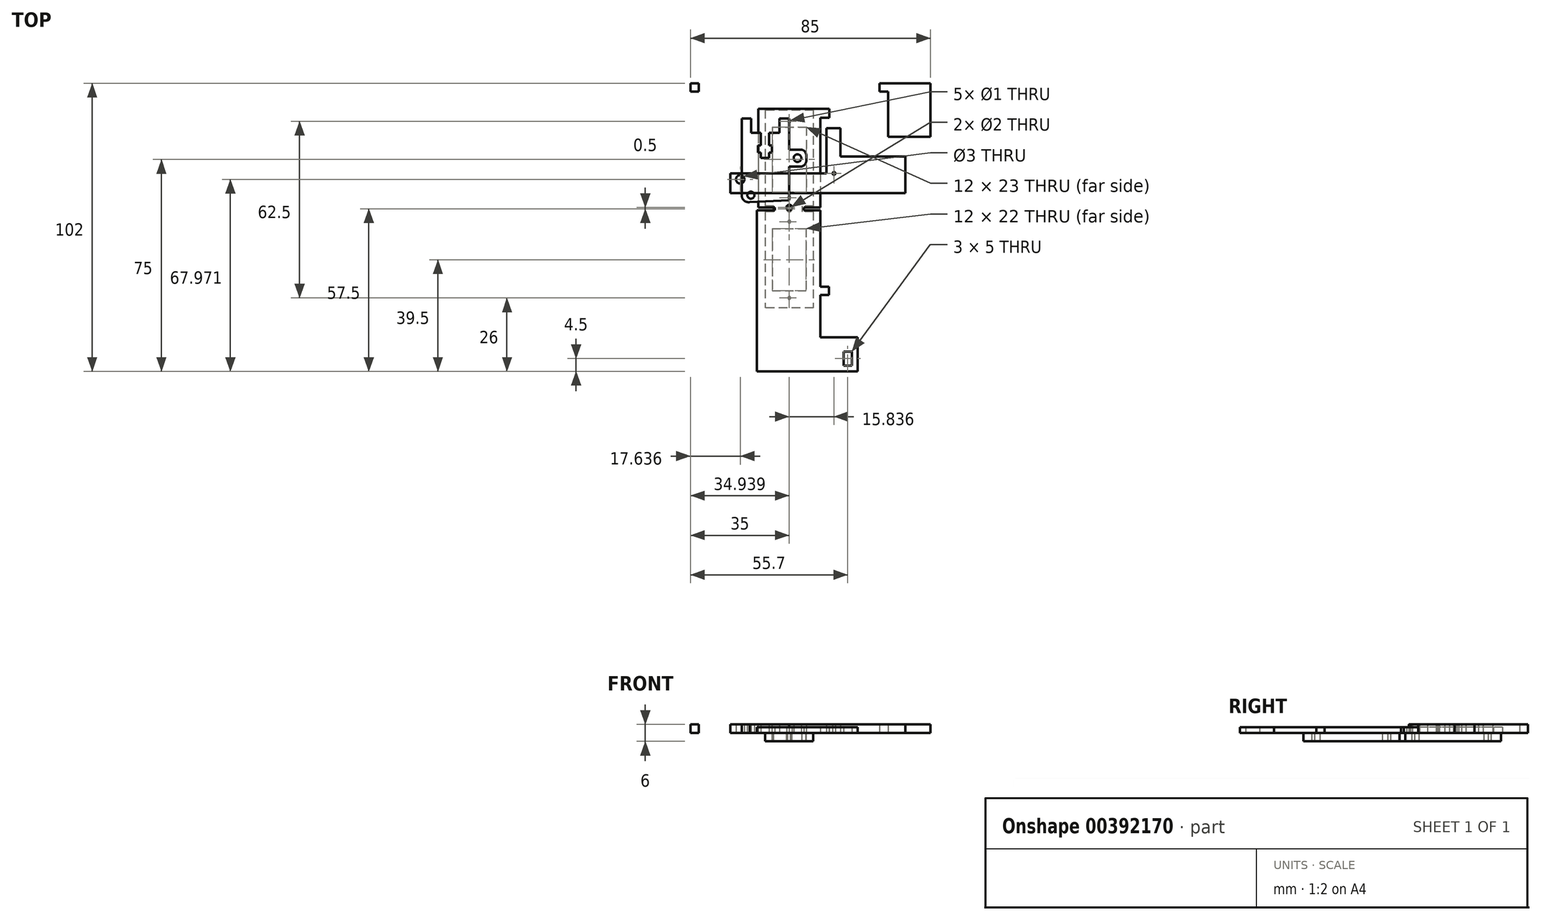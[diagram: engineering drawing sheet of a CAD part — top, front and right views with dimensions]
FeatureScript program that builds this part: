
annotation { "Feature Type Name" : "Feature", "Feature Type Description" : "" }
export const myFeature = defineFeature(function(context is Context, id is Id, definition is map)
    precondition{}
    {
        {
            var Q0;
            Q0=qCreatedBy(makeId("Top.planeOp"),FACE);
            var sketch = newSketch(context, id + "F0", { "sketchPlane" : qUnion([Q0])});
            skLineSegment(sketch, "E0.bottom", {"start": v(11, 17.5) * mm, "end": v(-11, 17.5) * mm});
            skLineSegment(sketch, "E0.top", {"start": v(11, -17.5) * mm, "end": v(-11, -17.5) * mm});
            skLineSegment(sketch, "E0.left", {"start": v(11, 17.5) * mm, "end": v(11, -17.5) * mm});
            skLineSegment(sketch, "E0.right", {"start": v(-11, 17.5) * mm, "end": v(-11, -17.5) * mm});
            skPoint(sketch, "E0.middle", {"position": v(0, 0) * mm});
            skLineSegment(sketch, "E1.bottom", {"start": v(11, 17.5) * mm, "end": v(14.2, 17.5) * mm});
            skLineSegment(sketch, "E1.top", {"start": v(11, 14.3) * mm, "end": v(14.2, 14.3) * mm});
            skLineSegment(sketch, "E1.left", {"start": v(11, 17.5) * mm, "end": v(11, 14.3) * mm});
            skLineSegment(sketch, "E1.right", {"start": v(14.2, 17.5) * mm, "end": v(14.2, 14.3) * mm});
            skLineSegment(sketch, "E2.bottom", {"start": v(5.1, -18.5) * mm, "end": v(-5.1, -18.5) * mm});
            skLineSegment(sketch, "E2.top", {"start": v(5.1, -16.5) * mm, "end": v(-5.1, -16.5) * mm});
            skLineSegment(sketch, "E2.left", {"start": v(5.1, -18.5) * mm, "end": v(5.1, -16.5) * mm});
            skLineSegment(sketch, "E2.right", {"start": v(-5.1, -18.5) * mm, "end": v(-5.1, -16.5) * mm});
            skPoint(sketch, "E2.middle", {"position": v(0, -17.5) * mm});
            skLineSegment(sketch, "E3.bottom", {"start": v(11, -18.5) * mm, "end": v(-11.53, -18.5) * mm});
            skLineSegment(sketch, "E3.top", {"start": v(11, -75.5) * mm, "end": v(-11.53, -75.5) * mm});
            skLineSegment(sketch, "E3.left", {"start": v(11, -18.5) * mm, "end": v(11, -75.5) * mm});
            skLineSegment(sketch, "E3.right", {"start": v(-11.53, -18.5) * mm, "end": v(-11.53, -75.5) * mm});
            skLineSegment(sketch, "E4.bottom", {"start": v(11, -75.5) * mm, "end": v(24.2, -75.5) * mm});
            skLineSegment(sketch, "E4.top", {"start": v(11, -63.5) * mm, "end": v(24.2, -63.5) * mm});
            skLineSegment(sketch, "E4.left", {"start": v(11, -75.5) * mm, "end": v(11, -63.5) * mm});
            skLineSegment(sketch, "E4.right", {"start": v(24.2, -75.5) * mm, "end": v(24.2, -63.5) * mm});
            skLineSegment(sketch, "E5.bottom", {"start": v(11, -45.5) * mm, "end": v(14, -45.5) * mm});
            skLineSegment(sketch, "E5.top", {"start": v(11, -48.5) * mm, "end": v(14, -48.5) * mm});
            skLineSegment(sketch, "E5.left", {"start": v(11, -45.5) * mm, "end": v(11, -48.5) * mm});
            skLineSegment(sketch, "E5.right", {"start": v(14, -45.5) * mm, "end": v(14, -48.5) * mm});
            skLineSegment(sketch, "E6.bottom", {"start": v(22.2, -73.5) * mm, "end": v(19.2, -73.5) * mm});
            skLineSegment(sketch, "E6.top", {"start": v(22.2, -68.5) * mm, "end": v(19.2, -68.5) * mm});
            skLineSegment(sketch, "E6.left", {"start": v(22.2, -73.5) * mm, "end": v(22.2, -68.5) * mm});
            skLineSegment(sketch, "E6.right", {"start": v(19.2, -73.5) * mm, "end": v(19.2, -68.5) * mm});
            skPoint(sketch, "E6.middle", {"position": v(20.7, -71) * mm});
            skCircle(sketch, "E7", {"center": v(0, -17.5) * mm, "radius": 1 * mm});
            skSolve(sketch);
        }
        {
            var Q0;
            Q0=makeQuery(id+"F0.imprint","IMPRINT",FACE,{"disambiguationData":[TD([[makeQuery(id+"F0.imprint","IMPRINT",EDGE,{"derivedFrom":sQuery(id+"F0.wireOp",EDGE,"E3.top")}),-1.0]])]});
            var Q1;
            Q1=makeQuery(id+"F0.imprint","IMPRINT",FACE,{"disambiguationData":[TD([[makeQuery(id+"F0.imprint","IMPRINT",EDGE,{"derivedFrom":sQuery(id+"F0.wireOp",EDGE,"E4.bottom")}),1.0]])]});
            var Q2;
            Q2=makeQuery(id+"F0.imprint","IMPRINT",FACE,{"disambiguationData":[TD([[makeQuery(id+"F0.imprint","IMPRINT",EDGE,{"derivedFrom":sQuery(id+"F0.wireOp",EDGE,"E5.bottom")}),-1.0]])]});
            var Q3;
            Q3=makeQuery(id+"F0.imprint","IMPRINT",FACE,{"disambiguationData":[TD([[makeQuery(id+"F0.imprint","IMPRINT",EDGE,{"derivedFrom":sQuery(id+"F0.wireOp",EDGE,"E0.bottom")}),1.0]])]});
            var Q4;
            Q4=makeQuery(id+"F0.imprint","IMPRINT",FACE,{"disambiguationData":[TD([[makeQuery(id+"F0.imprint","IMPRINT",EDGE,{"derivedFrom":sQuery(id+"F0.wireOp",EDGE,"E1.bottom")}),-1.0]])]});
            var Q5;
            {var subQ0=sQuery(id+"F0.wireOp",EDGE,"E2.left");var subQ1=sQuery(id+"F0.wireOp",EDGE,"E0.top");var subQ2=makeQuery(id+"F0.imprint","INTERSECT",VERTEX,{"derivedFrom":[subQ1,subQ0]});Q5=makeQuery(id+"F0.imprint","IMPRINT",FACE,{"disambiguationData":[TD([[makeQuery(id+"F0.imprint","IMPRINT",EDGE,{"disambiguationData":[TD([[subQ2,-1.0]])],"derivedFrom":subQ1}),1.0]])]});}
            var Q6;
            {var subQ0=sQuery(id+"F0.wireOp",EDGE,"E2.left");var subQ1=sQuery(id+"F0.wireOp",EDGE,"E0.top");var subQ2=makeQuery(id+"F0.imprint","INTERSECT",VERTEX,{"derivedFrom":[subQ1,subQ0]});Q6=makeQuery(id+"F0.imprint","IMPRINT",FACE,{"disambiguationData":[TD([[makeQuery(id+"F0.imprint","IMPRINT",EDGE,{"disambiguationData":[TD([[subQ2,-1.0]])],"derivedFrom":subQ1}),-1.0]])]});}
            var Q7;
            {var subQ0=sQuery(id+"F0.wireOp",EDGE,"E2.right");var subQ1=sQuery(id+"F0.wireOp",EDGE,"E0.top");var subQ2=makeQuery(id+"F0.imprint","INTERSECT",VERTEX,{"derivedFrom":[subQ1,subQ0]});Q7=makeQuery(id+"F0.imprint","IMPRINT",FACE,{"disambiguationData":[TD([[makeQuery(id+"F0.imprint","IMPRINT",EDGE,{"disambiguationData":[TD([[subQ2,1.0]])],"derivedFrom":subQ1}),1.0]])]});}
            var Q8;
            {var subQ0=sQuery(id+"F0.wireOp",EDGE,"E2.right");var subQ1=sQuery(id+"F0.wireOp",EDGE,"E0.top");var subQ2=makeQuery(id+"F0.imprint","INTERSECT",VERTEX,{"derivedFrom":[subQ1,subQ0]});Q8=makeQuery(id+"F0.imprint","IMPRINT",FACE,{"disambiguationData":[TD([[makeQuery(id+"F0.imprint","IMPRINT",EDGE,{"disambiguationData":[TD([[subQ2,1.0]])],"derivedFrom":subQ1}),-1.0]])]});}
            extrude(context, id + "F1", {"entities" : qUnion([Q0, Q1, Q2, Q3, Q4, Q5, Q6, Q7, Q8]), "depth" : 2 * mm});
        }
        {
            var Q0;
            Q0=qCreatedBy(makeId("Top.planeOp"),FACE);
            var sketch = newSketch(context, id + "F2", { "sketchPlane" : qUnion([Q0])});
            skLineSegment(sketch, "E8.top", {"start": v(35, 26.5) * mm, "end": v(-35, 26.5) * mm});
            skLineSegment(sketch, "E8.left", {"start": v(35, -26.5) * mm, "end": v(35, 26.5) * mm});
            skLineSegment(sketch, "E8.right", {"start": v(-35, -26.5) * mm, "end": v(-35, 26.5) * mm});
            skPoint(sketch, "E8.middle", {"position": v(0, 0) * mm});
            skLineSegment(sketch, "E9.bottom", {"start": v(35, 26.5) * mm, "end": v(50, 26.5) * mm});
            skLineSegment(sketch, "E9.top", {"start": v(35, 7.5) * mm, "end": v(50, 7.5) * mm});
            skLineSegment(sketch, "E9.left", {"start": v(35, 26.5) * mm, "end": v(35, 7.5) * mm});
            skLineSegment(sketch, "E9.right", {"start": v(50, 26.5) * mm, "end": v(50, 7.5) * mm});
            skLineSegment(sketch, "E10.bottom", {"start": v(-35, 26.5) * mm, "end": v(-32, 26.5) * mm});
            skLineSegment(sketch, "E10.top", {"start": v(-35, 23.5) * mm, "end": v(-32, 23.5) * mm});
            skLineSegment(sketch, "E10.left", {"start": v(-35, 26.5) * mm, "end": v(-35, 23.5) * mm});
            skLineSegment(sketch, "E10.right", {"start": v(-32, 26.5) * mm, "end": v(-32, 23.5) * mm});
            skLineSegment(sketch, "E11", {"start": v(-35, -26.5) * mm, "end": v(35, -26.5) * mm});
            skLineSegment(sketch, "E12.bottom", {"start": v(2, -26.5) * mm, "end": v(5, -26.5) * mm});
            skLineSegment(sketch, "E12.top", {"start": v(2, -23.5) * mm, "end": v(5, -23.5) * mm});
            skLineSegment(sketch, "E12.left", {"start": v(2, -26.5) * mm, "end": v(2, -23.5) * mm});
            skLineSegment(sketch, "E12.right", {"start": v(5, -26.5) * mm, "end": v(5, -23.5) * mm});
            skLineSegment(sketch, "E13.bottom", {"start": v(35, 26.5) * mm, "end": v(32, 26.5) * mm});
            skLineSegment(sketch, "E14.bottom", {"start": v(32, 26.5) * mm, "end": v(35, 26.5) * mm});
            skLineSegment(sketch, "E14.top", {"start": v(32, 23.5) * mm, "end": v(35, 23.5) * mm});
            skLineSegment(sketch, "E14.left", {"start": v(32, 26.5) * mm, "end": v(32, 23.5) * mm});
            skLineSegment(sketch, "E14.right", {"start": v(35, 26.5) * mm, "end": v(35, 23.5) * mm});
            skSolve(sketch);
        }
        {
            var Q0;
            Q0=makeQuery(id+"F2.imprint","IMPRINT",FACE,{"disambiguationData":[TD([[makeQuery(id+"F2.imprint","IMPRINT",EDGE,{"derivedFrom":sQuery(id+"F2.wireOp",EDGE,"E9.bottom")}),-1.0]])]});
            var Q1;
            Q1=makeQuery(id+"F2.imprint","IMPRINT",FACE,{"disambiguationData":[TD([[makeQuery(id+"F2.imprint","IMPRINT",EDGE,{"derivedFrom":sQuery(id+"F2.wireOp",EDGE,"E13.bottom")}),-1.0]])]});
            var Q2;
            Q2=makeQuery(id+"F2.imprint","IMPRINT",FACE,{"disambiguationData":[TD([[makeQuery(id+"F2.imprint","IMPRINT",EDGE,{"derivedFrom":sQuery(id+"F2.wireOp",EDGE,"E8.top")}),1.0]])]});
            extrude(context, id + "F3", {"entities" : qUnion([Q0, Q1, Q2]), "depth" : 3 * mm});
        }
        {
            var Q0;
            Q0=qCreatedBy(makeId("Top.planeOp"),FACE);
            var sketch = newSketch(context, id + "F4", { "sketchPlane" : qUnion([Q0])});
            skLineSegment(sketch, "E15.bottom", {"start": v(8.5, 17) * mm, "end": v(-8.5, 17) * mm});
            skLineSegment(sketch, "E15.top", {"start": v(8.5, -17) * mm, "end": v(-8.5, -17) * mm});
            skLineSegment(sketch, "E15.left", {"start": v(8.5, 17) * mm, "end": v(8.5, -17) * mm});
            skLineSegment(sketch, "E15.right", {"start": v(-8.5, 17) * mm, "end": v(-8.5, -17) * mm});
            skPoint(sketch, "E15.middle", {"position": v(0, 0) * mm});
            skLineSegment(sketch, "E16.bottom", {"start": v(-6, 11) * mm, "end": v(6, 11) * mm});
            skLineSegment(sketch, "E16.top", {"start": v(-6, -12) * mm, "end": v(6, -12) * mm});
            skLineSegment(sketch, "E16.left", {"start": v(-6, 11) * mm, "end": v(-6, -12) * mm});
            skLineSegment(sketch, "E16.right", {"start": v(6, 11) * mm, "end": v(6, -12) * mm});
            skPoint(sketch, "E17.MirrorP", {"position": v(0, -34) * mm});
            skCircle(sketch, "E18", {"center": v(0, 13) * mm, "radius": 0.5 * mm});
            skCircle(sketch, "E19", {"center": v(0, -14) * mm, "radius": 0.5 * mm});
            skLineSegment(sketch, "E20.bottom", {"start": v(4.5, -17) * mm, "end": v(-5.5, -17) * mm});
            skLineSegment(sketch, "E20.top", {"start": v(4.5, -19) * mm, "end": v(-5.5, -19) * mm});
            skLineSegment(sketch, "E20.left", {"start": v(4.5, -17) * mm, "end": v(4.5, -19) * mm});
            skLineSegment(sketch, "E20.right", {"start": v(-5.5, -17) * mm, "end": v(-5.5, -19) * mm});
            skLineSegment(sketch, "E21.bottom", {"start": v(8.5, -19) * mm, "end": v(-8.5, -19) * mm});
            skLineSegment(sketch, "E21.top", {"start": v(8.5, -53) * mm, "end": v(-8.5, -53) * mm});
            skLineSegment(sketch, "E21.left", {"start": v(8.5, -19) * mm, "end": v(8.5, -53) * mm});
            skLineSegment(sketch, "E21.right", {"start": v(-8.5, -19) * mm, "end": v(-8.5, -53) * mm});
            skLineSegment(sketch, "E22.bottom", {"start": v(-6.06, -25) * mm, "end": v(5.94, -25) * mm});
            skLineSegment(sketch, "E22.top", {"start": v(-6.06, -47) * mm, "end": v(5.94, -47) * mm});
            skLineSegment(sketch, "E22.left", {"start": v(-6.06, -25) * mm, "end": v(-6.06, -47) * mm});
            skLineSegment(sketch, "E22.right", {"start": v(5.94, -25) * mm, "end": v(5.94, -47) * mm});
            skCircle(sketch, "E23", {"center": v(0, -22.5) * mm, "radius": 0.5 * mm});
            skCircle(sketch, "E24", {"center": v(0, -49.5) * mm, "radius": 0.5 * mm});
            skCircle(sketch, "E25", {"center": v(0, -18) * mm, "radius": 1 * mm});
            skSolve(sketch);
        }
        {
            var Q0;
            Q0=makeQuery(id+"F4.imprint","IMPRINT",FACE,{"disambiguationData":[TD([[makeQuery(id+"F4.imprint","IMPRINT",EDGE,{"derivedFrom":sQuery(id+"F4.wireOp",EDGE,"E15.bottom")}),1.0]])]});
            var Q1;
            {var subQ0=sQuery(id+"F4.wireOp",EDGE,"E20.left");Q1=makeQuery(id+"F4.imprint","IMPRINT",FACE,{"disambiguationData":[TD([[makeQuery(id+"F4.imprint","IMPRINT",EDGE,{"derivedFrom":subQ0}),-1.0]])]});}
            var Q2;
            {var subQ0=sQuery(id+"F4.wireOp",EDGE,"E20.right");Q2=makeQuery(id+"F4.imprint","IMPRINT",FACE,{"disambiguationData":[TD([[makeQuery(id+"F4.imprint","IMPRINT",EDGE,{"derivedFrom":subQ0}),1.0]])]});}
            var Q3;
            Q3=makeQuery(id+"F4.imprint","IMPRINT",FACE,{"disambiguationData":[TD([[makeQuery(id+"F4.imprint","IMPRINT",EDGE,{"derivedFrom":sQuery(id+"F4.wireOp",EDGE,"E21.top")}),-1.0]])]});
            extrude(context, id + "F5", {"entities" : qUnion([Q0, Q1, Q2, Q3]), "oppositeDirection" : true, "depth" : 3 * mm});
        }
        {
            var Q0;
            Q0=qCreatedBy(makeId("Top.planeOp"),FACE);
            var sketch = newSketch(context, id + "F6", { "sketchPlane" : qUnion([Q0])});
            skLineSegment(sketch, "E26", {"start": v(-16.85, 14) * mm, "end": v(0, 14) * mm});
            skLineSegment(sketch, "E27", {"start": v(0, 14) * mm, "end": v(0, -13.75) * mm});
            skLineSegment(sketch, "E28", {"start": v(-16.85, 14) * mm, "end": v(-16.85, -13.14) * mm});
            skPoint(sketch, "E29.visualSharp", {"position": v(-16.85, -16) * mm});
            skArc(sketch, "E29.filletArc", {"start": v(-16.85, -13.14) * mm, "mid": v(-16, -15.02) * mm, "end": v(-14.02, -15.62) * mm});
            skCircle(sketch, "E30", {"center": v(-13.6, -13.14) * mm, "radius": 1.25 * mm});
            skLineSegment(sketch, "E31.bottom", {"start": v(-13.5, 14) * mm, "end": v(-3.5, 14) * mm});
            skLineSegment(sketch, "E31.top", {"start": v(-13.5, 9) * mm, "end": v(-3.5, 9) * mm});
            skLineSegment(sketch, "E31.left", {"start": v(-13.5, 14) * mm, "end": v(-13.5, 9) * mm});
            skLineSegment(sketch, "E31.right", {"start": v(-3.5, 14) * mm, "end": v(-3.5, 9) * mm});
            skLineSegment(sketch, "E32.bottom", {"start": v(-7.1, 9) * mm, "end": v(-10.1, 9) * mm});
            skLineSegment(sketch, "E32.top", {"start": v(-7.1, 0) * mm, "end": v(-10.1, 0) * mm});
            skLineSegment(sketch, "E32.left", {"start": v(-7.1, 9) * mm, "end": v(-7.1, 0) * mm});
            skLineSegment(sketch, "E32.right", {"start": v(-10.1, 9) * mm, "end": v(-10.1, 0) * mm});
            skPoint(sketch, "E33.oppositeSnap0", {"position": v(-7.1, 4.5) * mm});
            skLineSegment(sketch, "E33.bottom", {"start": v(-7.1, 2) * mm, "end": v(-6.1, 2) * mm});
            skLineSegment(sketch, "E33.top", {"start": v(-7.1, 4.5) * mm, "end": v(-6.1, 4.5) * mm});
            skLineSegment(sketch, "E33.left", {"start": v(-7.1, 2) * mm, "end": v(-7.1, 4.5) * mm});
            skLineSegment(sketch, "E33.right", {"start": v(-6.1, 2) * mm, "end": v(-6.1, 4.5) * mm});
            skLineSegment(sketch, "E34.bottom", {"start": v(-10.1, 4.5) * mm, "end": v(-11.1, 4.5) * mm});
            skLineSegment(sketch, "E34.top", {"start": v(-10.1, 2) * mm, "end": v(-11.1, 2) * mm});
            skLineSegment(sketch, "E34.left", {"start": v(-10.1, 4.5) * mm, "end": v(-10.1, 2) * mm});
            skLineSegment(sketch, "E34.right", {"start": v(-11.1, 4.5) * mm, "end": v(-11.1, 2) * mm});
            skLineSegment(sketch, "E35", {"start": v(-10.1, 4.5) * mm, "end": v(-7.1, 4.5) * mm});
            skLineSegment(sketch, "E36", {"start": v(-10.1, 2) * mm, "end": v(-7.1, 2) * mm});
            skLineSegment(sketch, "E37.bottom", {"start": v(0, 3) * mm, "end": v(4, 3) * mm});
            skLineSegment(sketch, "E37.top", {"start": v(0, -3) * mm, "end": v(4, -3) * mm});
            skLineSegment(sketch, "E37.left", {"start": v(0, 3) * mm, "end": v(0, -3) * mm});
            skLineSegment(sketch, "E37.right", {"start": v(6, 1) * mm, "end": v(6, -1) * mm});
            skLineSegment(sketch, "E38", {"start": v(-14.02, -15.62) * mm, "end": v(0, -15) * mm});
            skLineSegment(sketch, "E39", {"start": v(0, -15) * mm, "end": v(0, -13.75) * mm});
            skPoint(sketch, "E40.visualSharp", {"position": v(6, -3) * mm});
            skArc(sketch, "E40.filletArc", {"start": v(4, -3) * mm, "mid": v(5.41, -2.41) * mm, "end": v(6, -1) * mm});
            skPoint(sketch, "E41.visualSharp", {"position": v(6, 3) * mm});
            skArc(sketch, "E41.filletArc", {"start": v(6, 1) * mm, "mid": v(5.41, 2.41) * mm, "end": v(4, 3) * mm});
            skCircle(sketch, "E42", {"center": v(2.9, 0) * mm, "radius": 1.35 * mm});
            skSolve(sketch);
        }
        {
            var Q0;
            Q0=makeQuery(id+"F6.imprint","IMPRINT",FACE,{"disambiguationData":[TD([[makeQuery(id+"F6.imprint","IMPRINT",EDGE,{"derivedFrom":sQuery(id+"F6.wireOp",EDGE,"E37.bottom")}),-1.0]])]});
            var Q1;
            {var subQ22=sQuery(id+"F6.wireOp",EDGE,"E28");Q1=makeQuery(id+"F6.imprint","IMPRINT",FACE,{"disambiguationData":[TD([[makeQuery(id+"F6.imprint","IMPRINT",EDGE,{"derivedFrom":subQ22}),1.0]])]});}
            extrude(context, id + "F7", {"entities" : qUnion([Q0, Q1]), "depth" : 3 * mm});
        }
        {
            var Q0;
            Q0=qCreatedBy(makeId("Top.planeOp"),FACE);
            var sketch = newSketch(context, id + "F8", { "sketchPlane" : qUnion([Q0])});
            skLineSegment(sketch, "E43.bottom", {"start": v(-20.86, -5.43) * mm, "end": v(18.14, -5.43) * mm});
            skLineSegment(sketch, "E43.top", {"start": v(-20.86, -12.43) * mm, "end": v(18.14, -12.43) * mm});
            skLineSegment(sketch, "E43.left", {"start": v(-20.86, -5.43) * mm, "end": v(-20.86, -12.43) * mm});
            skLineSegment(sketch, "E43.right", {"start": v(18.14, -5.43) * mm, "end": v(18.14, -12.43) * mm});
            skCircle(sketch, "E44", {"center": v(-17.36, -7.53) * mm, "radius": 1.5 * mm});
            skCircle(sketch, "E45", {"center": v(15.84, -5.43) * mm, "radius": 0.5 * mm});
            skLineSegment(sketch, "E46.bottom", {"start": v(18.14, -5.43) * mm, "end": v(13.14, -5.43) * mm});
            skLineSegment(sketch, "E46.top", {"start": v(18.14, 10.57) * mm, "end": v(13.14, 10.57) * mm});
            skLineSegment(sketch, "E46.left", {"start": v(18.14, -5.43) * mm, "end": v(18.14, 10.57) * mm});
            skLineSegment(sketch, "E46.right", {"start": v(13.14, -5.43) * mm, "end": v(13.14, 10.57) * mm});
            skLineSegment(sketch, "E47.bottom", {"start": v(13.14, 10.57) * mm, "end": v(16.14, 10.57) * mm});
            skLineSegment(sketch, "E47.top", {"start": v(13.14, 13.57) * mm, "end": v(16.14, 13.57) * mm});
            skLineSegment(sketch, "E47.left", {"start": v(13.14, 10.57) * mm, "end": v(13.14, 13.57) * mm});
            skLineSegment(sketch, "E47.right", {"start": v(16.14, 10.57) * mm, "end": v(16.14, 13.57) * mm});
            skLineSegment(sketch, "E48.bottom", {"start": v(18.14, -12.43) * mm, "end": v(18.14, -12.43) * mm});
            skLineSegment(sketch, "E48.top", {"start": v(18.14, 10.57) * mm, "end": v(18.14, 10.57) * mm});
            skLineSegment(sketch, "E48.left", {"start": v(18.14, -12.43) * mm, "end": v(18.14, 10.57) * mm});
            skLineSegment(sketch, "E49.bottom", {"start": v(18.14, -12.43) * mm, "end": v(66.14, -12.43) * mm});
            skLineSegment(sketch, "E49.top", {"start": v(18.14, 10.57) * mm, "end": v(66.14, 10.57) * mm});
            skLineSegment(sketch, "E49.right", {"start": v(66.14, -12.43) * mm, "end": v(66.14, 10.57) * mm});
            skLineSegment(sketch, "E50.bottom", {"start": v(18.14, -12.43) * mm, "end": v(41.14, -12.43) * mm});
            skLineSegment(sketch, "E50.top", {"start": v(18.14, 0.57) * mm, "end": v(41.14, 0.57) * mm});
            skLineSegment(sketch, "E50.left", {"start": v(18.14, -12.43) * mm, "end": v(18.14, 0.57) * mm});
            skLineSegment(sketch, "E50.right", {"start": v(41.14, -12.43) * mm, "end": v(41.14, 0.57) * mm});
            skLineSegment(sketch, "E51.bottom", {"start": v(66.14, 3.57) * mm, "end": v(63.14, 3.57) * mm});
            skLineSegment(sketch, "E51.top", {"start": v(66.14, -7.43) * mm, "end": v(63.14, -7.43) * mm});
            skLineSegment(sketch, "E51.left", {"start": v(66.14, 3.57) * mm, "end": v(66.14, -7.43) * mm});
            skLineSegment(sketch, "E51.right", {"start": v(63.14, 3.57) * mm, "end": v(63.14, -7.43) * mm});
            skPoint(sketch, "E52.firstSnap1", {"position": v(66.14, -0.93) * mm});
            skLineSegment(sketch, "E53", {"start": v(51.14, -0.07) * mm, "end": v(51.14, -3.07) * mm});
            skLineSegment(sketch, "E54", {"start": v(51.14, -3.07) * mm, "end": v(63.14, -3.07) * mm});
            skLineSegment(sketch, "E55.bottom", {"start": v(56.14, -3.07) * mm, "end": v(59.14, -3.07) * mm});
            skLineSegment(sketch, "E55.top", {"start": v(56.14, -4.07) * mm, "end": v(59.14, -4.07) * mm});
            skLineSegment(sketch, "E55.left", {"start": v(56.14, -3.07) * mm, "end": v(56.14, -4.07) * mm});
            skLineSegment(sketch, "E55.right", {"start": v(59.14, -3.07) * mm, "end": v(59.14, -4.07) * mm});
            skPoint(sketch, "E56.oppositeSnap0", {"position": v(59.14, -3.57) * mm});
            skLineSegment(sketch, "E57", {"start": v(51.14, -0.07) * mm, "end": v(63.14, -0.07) * mm});
            skLineSegment(sketch, "E58.bottom", {"start": v(56.14, -0.07) * mm, "end": v(59.14, -0.07) * mm});
            skLineSegment(sketch, "E58.top", {"start": v(56.14, 0.93) * mm, "end": v(59.14, 0.93) * mm});
            skLineSegment(sketch, "E58.left", {"start": v(56.14, -0.07) * mm, "end": v(56.14, 0.93) * mm});
            skLineSegment(sketch, "E58.right", {"start": v(59.14, -0.07) * mm, "end": v(59.14, 0.93) * mm});
            skCircle(sketch, "E59", {"center": v(43.64, -5.43) * mm, "radius": 0.5 * mm});
            skSolve(sketch);
        }
        {
            var Q0;
            Q0=makeQuery(id+"F8.imprint","IMPRINT",FACE,{"disambiguationData":[TD([[makeQuery(id+"F8.imprint","IMPRINT",EDGE,{"derivedFrom":sQuery(id+"F8.wireOp",EDGE,"E47.bottom")}),1.0]])]});
            var Q1;
            {var subQ1=sQuery(id+"F8.wireOp",EDGE,"E43.bottom");Q1=makeQuery(id+"F8.imprint","IMPRINT",FACE,{"disambiguationData":[TD([[makeQuery(id+"F8.imprint","IMPRINT",EDGE,{"derivedFrom":subQ1}),-1.0]])]});}
            var Q2;
            Q2=makeQuery(id+"F8.imprint","IMPRINT",FACE,{"disambiguationData":[TD([[makeQuery(id+"F8.imprint","IMPRINT",EDGE,{"derivedFrom":sQuery(id+"F8.wireOp",EDGE,"E46.top")}),1.0]])]});
            var Q3;
            {var subQ10=sQuery(id+"F8.wireOp",EDGE,"E49.bottom");Q3=makeQuery(id+"F8.imprint","IMPRINT",FACE,{"disambiguationData":[TD([[makeQuery(id+"F8.imprint","IMPRINT",EDGE,{"derivedFrom":subQ10}),1.0]])]});}
            extrude(context, id + "F9", {"entities" : qUnion([Q0, Q1, Q2, Q3]), "depth" : 3 * mm});
        }
    });
